# Revit family: Bearing Block
name_source: partatom
category: Generic Models
revit_build: Autodesk Revit MEP 2012 (Build: 20110309_2315)
units: mm (PartAtom-declared; Revit-internal decimal feet)

## types (1)
- Bearing Block
    Bearing_Block Inside Edge Offset = 1.25 "
    Bearing_Block_Web_Thickness = 0.5 "
    Edge_Radius = 0.25 "
    Inside_Web_Rail_Clear = 0.25 "
    Material = <By Category>
    Mounting_Hole_CtoC = 3 "
    Mounting_Hole_Diameter = 0.313 "
    Mounting_Hole_Radius = 0.157 "
    Rail_Height = 4 "
    Rail_Thickness = 1.25 "
    Roller_Hole_CtoC = 2 "
    Side_Roller_Hole_Diameter = 0.625 "
    Side_Roller_Hole_Radius = 0.313 "
    Side_Roller_Radius = 0.75 "
    Side_Roller_Web_Edge_Thickness = 0.75 "
    Side_Web_Edge_Offset = 0.625 "
    Side_Web_Width = 1.5 "
    Siesmic_Web_Location = 4.75 "
    Siesmic_Web_Offset = 0.25 "
    Top_Roller_Hole_Diameter = 0.625 "
    Top_Roller_Hole_Radius = 0.313 "
    Top_Roller_Radius = 0.75 "
    Top_Roller_Web_Edge_Thickness = 0.75 "
    Top_Web_Edge_Offset = 0.625 "
    Top_Web_Notch_Length = 2 "
    Top_Web_Rail_Clear = 0.25 "
    Top_Web_Width = 1.5 "

## geometry (parser evidence)
native form markers: Blend x2, Sweep x6
no freeform markers — native parametric forms only
